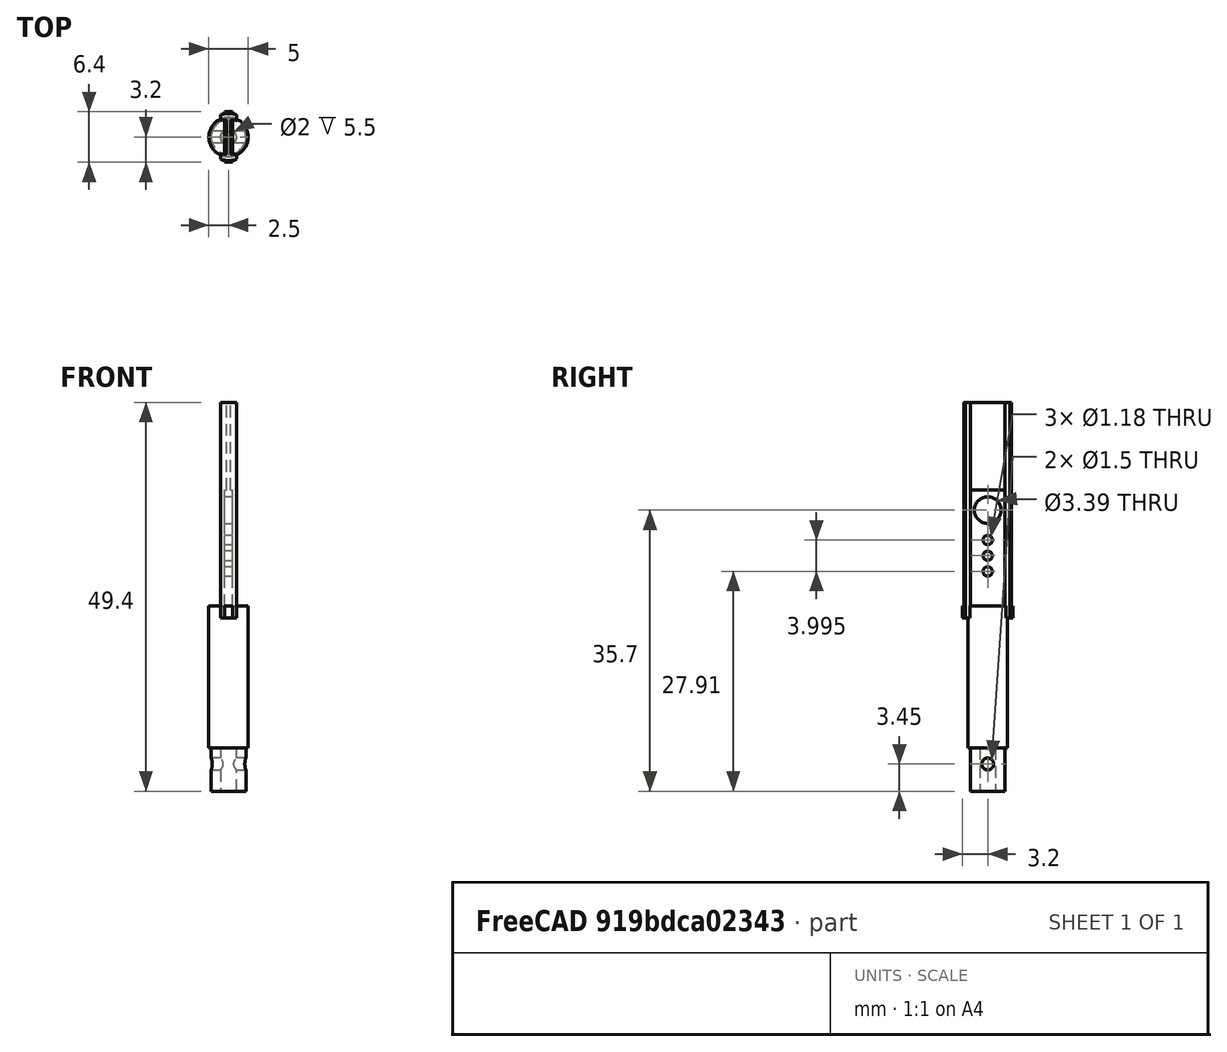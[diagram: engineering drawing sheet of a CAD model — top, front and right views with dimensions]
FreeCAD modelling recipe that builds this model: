
FCSTD DOCUMENT  (FreeCAD 0.21R33675 (Git))
Label: temholder2
License: All rights reserved
LicenseURL: http://en.wikipedia.org/wiki/All_rights_reserved
objects: TechDraw::DrawViewDimension×22, Part::Cylinder×10, TechDraw::DrawProjGroupItem×10, Part::Cut×8, Part::Box×7, Part::MultiFuse×6, TechDraw::DrawSVGTemplate×2, TechDraw::DrawProjGroup×2, TechDraw::DrawPage×2, Part::MultiCommon×1
note: 32 computed .brp shape members not serialized (recipe doc carries the construction recipe); baked Part::Feature solids carry a one-line shape summary decoded from their .brp

FEATURE [Part::Cylinder] Cylinder  label="Zylinder"
  Angle = 360
  AttacherType = Attacher::AttachEngine3D
  FirstAngle = 0
  Height = 21.5
  Placement = pos=(0,0,-0.5) rot=(0,0,1;0rad)
  Radius = 2.2
  SecondAngle = 0
FEATURE [Part::Cylinder] Cylinder001  label="Zylinder001"
  Angle = 360
  AttacherType = Attacher::AttachEngine3D
  FirstAngle = 0
  Height = 18
  Placement = pos=(0,0,5) rot=(0,0,1;0rad)
  Radius = 2.5
  SecondAngle = 0
FEATURE [Part::Cylinder] Cylinder002  label="Zylinder002"
  Angle = 360
  AttacherType = Attacher::AttachEngine3D
  FirstAngle = 0
  Height = 6.2
  Placement = pos=(-3.25,0,2.95) rot=(0,1,0;1.5708rad)
  Radius = 0.75
  SecondAngle = 0
FEATURE [Part::MultiFuse] Fusion
  Shapes = -> [Cylinder,Cylinder001]
FEATURE [Part::Cut] Cut
  Base = -> Fusion
  Tool = -> Cylinder002
FEATURE [Part::Box] Box  label="Würfel"
  AttacherType = Attacher::AttachEngine3D
  Height = 27.9
  Length = 2
  Placement = pos=(-1,-5,21) rot=(0,0,1;0rad)
  Width = 10
FEATURE [Part::Cylinder] Cylinder003  label="BeamHole"
  Angle = 360
  AttacherType = Attacher::AttachEngine3D
  FirstAngle = 0
  Height = 2
  Placement = pos=(-1,0,35.2) rot=(0,1,0;1.5708rad)
  Radius = 1.1
  SecondAngle = 0
FEATURE [Part::Cylinder] Cylinder004  label="Zylinder004"
  Angle = 360
  AttacherType = Attacher::AttachEngine3D
  FirstAngle = 0
  Height = 27.4
  Placement = pos=(0,0,21.5) rot=(0,0,1;0rad)
  Radius = 3
  SecondAngle = 0
FEATURE [Part::MultiCommon] Common
  Shapes = -> [Cylinder004,Box]
FEATURE [Part::Cut] Cut001
  Base = -> Common
  Tool = -> Cylinder003
FEATURE [Part::Cylinder] Cylinder005  label="Zylinder005"
  Angle = 360
  AttacherType = Attacher::AttachEngine3D
  FirstAngle = 0
  Height = 5.5
  Placement = pos=(0,0,-0.5) rot=(0,0,1;0rad)
  Radius = 1
  SecondAngle = 0
FEATURE [Part::Cut] Cut002
  Base = -> Cut
  Tool = -> Cylinder005
FEATURE [Part::Cylinder] Cylinder006  label="ProbeHole"
  Angle = 360
  AttacherType = Attacher::AttachEngine3D
  FirstAngle = 0
  Height = 20
  Placement = pos=(-4,0,35.2) rot=(0,1,0;1.5708rad)
  Radius = 1.695
  SecondAngle = 0
FEATURE [Part::Cut] Cut003
  Base = -> Cut001
  Tool = -> Cylinder006
FEATURE [Part::Box] Box001  label="Würfel001"
  AttacherType = Attacher::AttachEngine3D
  Height = 27
  Length = 10
  Placement = pos=(1,-2.57,21) rot=(0,0,1;0rad)
  Width = 5.5
FEATURE [Part::Cut] Cut004
  Base = -> Cut003
  Tool = -> Box001
FEATURE [Part::MultiFuse] Fusion001
  Shapes = -> [Cut002,Cut004]
FEATURE [Part::Box] Box002  label="Würfel002"
  AttacherType = Attacher::AttachEngine3D
  Height = 1.5
  Length = 1
  Placement = pos=(-0.5,-3.2,21.5) rot=(0,0,1;0rad)
  Width = 6.4
FEATURE [Part::Box] Box003  label="Würfel003"
  AttacherType = Attacher::AttachEngine3D
  Height = 26
  Length = 10
  Placement = pos=(0.5,-2.19,23) rot=(0,0,1;0rad)
  Width = 4.37
FEATURE [Part::Box] Box004  label="Würfel004"
  AttacherType = Attacher::AttachEngine3D
  Height = 26
  Length = 10
  Placement = pos=(-10.5,-2.19,23) rot=(0,0,1;0rad)
  Width = 4.37
FEATURE [Part::MultiFuse] Fusion002  label="MirrorGrooves"
  Shapes = -> [Box004,Box003]
FEATURE [Part::Cut] Cut005
  Base = -> Fusion001
  Tool = -> Fusion002
FEATURE [Part::Cylinder] Cylinder007  label="M1_6__Thread1"
  Angle = 360
  AttacherType = Attacher::AttachEngine3D
  FirstAngle = 0
  Height = 50
  Placement = pos=(-4,0,31.405) rot=(0,1,0;1.5708rad)
  Radius = 0.59
  SecondAngle = 0
FEATURE [Part::Cylinder] Cylinder008  label="M1_6__Thread2"
  Angle = 360
  AttacherType = Attacher::AttachEngine3D
  FirstAngle = 0
  Height = 50
  Placement = pos=(-4,0,29.41) rot=(0,1,0;1.5708rad)
  Radius = 0.59
  SecondAngle = 0
FEATURE [Part::Box] Box005  label="Würfel005"
  AttacherType = Attacher::AttachEngine3D
  Height = 12
  Length = 10
  Placement = pos=(0.25,-2.19,36.77) rot=(0,0,1;0rad)
  Width = 4.37
FEATURE [Part::Box] Box006  label="Würfel006"
  AttacherType = Attacher::AttachEngine3D
  Height = 12
  Length = 10
  Placement = pos=(-10.25,-2.19,36.77) rot=(0,0,1;0rad)
  Width = 4.37
FEATURE [Part::MultiFuse] Fusion004
  Placement = pos=(0,0,1) rot=(0,0,1;0rad)
  Shapes = -> [Box005,Box006]
FEATURE [TechDraw::DrawSVGTemplate] Template
  EditableTexts = Designed_by_Name=Thomas Spielauer; Drawing_number=001; FC-Date=2023-05-22; FC-SC=2:1; FC-SH=2/2; FC-Title=TEM Mirror Holder; Subtitle=Version 2023-05-22
  Height = 210
  Orientation = 1
  Width = 297
FEATURE [TechDraw::DrawSVGTemplate] Template001
  EditableTexts = Designed_by_Name=Thomas Spielauer; Drawing_number=001; FC-Date=2023-05-22; FC-SC=3:2; FC-SH=2/2; FC-Title=TEM Mirror Holder; Subtitle=Version 2023-05-22
  Height = 210
  Orientation = 1
  Width = 297
FEATURE [Part::Cylinder] Cylinder009  label="M1_6__Thread3"
  Angle = 360
  AttacherType = Attacher::AttachEngine3D
  FirstAngle = 0
  Height = 50
  Placement = pos=(-4,0,27.41) rot=(0,1,0;1.5708rad)
  Radius = 0.59
  SecondAngle = 0
FEATURE [Part::MultiFuse] Fusion003  label="MirrorMountingHoles"
  Shapes = -> [Cylinder007,Cylinder008,Cylinder009]
FEATURE [Part::Cut] Cut006
  Base = -> Cut005
  Tool = -> Fusion003
FEATURE [Part::Cut] Cut007
  Base = -> Cut006
  Tool = -> Fusion004
FEATURE [Part::MultiFuse] Fusion005
  Shapes = -> [Cut007,Box002]
FEATURE [TechDraw::DrawProjGroupItem] ProjItem  label="Front"
  CoarseView = false
  Direction = (1,0,0)
  Focus = 100
  HardHidden = false
  IsoCount = 0
  IsoHidden = false
  IsoVisible = false
  LockPosition = true
  Perspective = false
  Rotation = 0
  RotationVector = (0,1,0)
  Scale = 2
  ScaleType = 2
  ScrubCount = 0
  SeamHidden = false
  SeamVisible = true
  SmoothHidden = false
  SmoothVisible = true
  Source = -> [Fusion005]
  Type = 0
  X = 0
  XDirection = (0,-2e-16,-1)
  Y = 0
FEATURE [TechDraw::DrawProjGroupItem] ProjItem001  label="Left"
  CoarseView = false
  Direction = (1e-16,2e-16,1)
  Focus = 100
  HardHidden = false
  IsoCount = 0
  IsoHidden = false
  IsoVisible = false
  LockPosition = false
  Perspective = false
  Rotation = 0
  RotationVector = (1,0,0)
  Scale = 2
  ScaleType = 2
  ScrubCount = 0
  SeamHidden = false
  SeamVisible = true
  SmoothHidden = false
  SmoothVisible = true
  Source = -> [Fusion005]
  Type = 1
  X = 54.4
  XDirection = (1,0,-1e-16)
  Y = 0
FEATURE [TechDraw::DrawProjGroupItem] ProjItem003  label="Right"
  CoarseView = false
  Direction = (1e-16,-2e-16,-1)
  Focus = 100
  HardHidden = false
  IsoCount = 0
  IsoHidden = false
  IsoVisible = false
  LockPosition = false
  Perspective = false
  Rotation = 0
  RotationVector = (1,0,0)
  Scale = 2
  ScaleType = 2
  ScrubCount = 0
  SeamHidden = false
  SeamVisible = true
  SmoothHidden = false
  SmoothVisible = true
  Source = -> [Fusion005]
  Type = 2
  X = -54.4
  XDirection = (-1,0,-1e-16)
  Y = 0
FEATURE [TechDraw::DrawProjGroupItem] ProjItem004  label="Bottom"
  CoarseView = false
  Direction = (0,-1,2e-16)
  Focus = 100
  HardHidden = false
  IsoCount = 0
  IsoHidden = false
  IsoVisible = false
  LockPosition = false
  Perspective = false
  Rotation = 0
  RotationVector = (1,0,0)
  ScaleType = 2
  ScrubCount = 0
  SeamHidden = false
  SeamVisible = true
  SmoothHidden = false
  SmoothVisible = true
  Source = -> [Fusion005]
  Type = 5
  X = 0
  XDirection = (0,-2e-16,-1)
  Y = 41.4
FEATURE [TechDraw::DrawProjGroup] ProjGroup
  Anchor = -> ProjItem
  AutoDistribute = true
  LockPosition = false
  ProjectionType = 0
  Rotation = 0
  Scale = 2
  ScaleType = 1
  Source = -> [Fusion005]
  Views = -> [ProjItem,ProjItem001,ProjItem003,ProjItem004]
  X = 148.5
  Y = 105
  spacingX = 0
  spacingY = 30
FEATURE [TechDraw::DrawViewDimension] Dimension
  AngleOverride = false
  Arbitrary = false
  ArbitraryTolerances = false
  EqualTolerance = true
  ExtensionAngle = 0
  FormatSpec = %.2w
  FormatSpecOverTolerance = %+.2w
  FormatSpecUnderTolerance = %+.2w
  Inverted = false
  LineAngle = 0
  LockPosition = false
  MeasureType = 1
  OverTolerance = 0
  References2D = -> [ProjItem004]
  Rotation = 0
  ScaleType = 0
  TheoreticalExact = false
  Type = 0
  UnderTolerance = 0
  X = -0.570385
  Y = 36.7256
FEATURE [TechDraw::DrawViewDimension] Dimension001
  AngleOverride = false
  Arbitrary = false
  ArbitraryTolerances = false
  EqualTolerance = true
  ExtensionAngle = 0
  FormatSpec = %.2w
  FormatSpecOverTolerance = %+.2w
  FormatSpecUnderTolerance = %+.2w
  Inverted = false
  LineAngle = 0
  LockPosition = false
  MeasureType = 1
  OverTolerance = 0
  References2D = -> [ProjItem004]
  Rotation = 0
  ScaleType = 0
  TheoreticalExact = false
  Type = 0
  UnderTolerance = 0
  X = 43.2488
  Y = 27.3992
FEATURE [TechDraw::DrawViewDimension] Dimension002
  AngleOverride = false
  Arbitrary = false
  ArbitraryTolerances = false
  EqualTolerance = true
  ExtensionAngle = 0
  FormatSpec = %.2w
  FormatSpecOverTolerance = %+.2w
  FormatSpecUnderTolerance = %+.2w
  Inverted = false
  LineAngle = 0
  LockPosition = false
  MeasureType = 1
  OverTolerance = 0
  References2D = -> [ProjItem004]
  Rotation = 0
  ScaleType = 0
  TheoreticalExact = false
  Type = 0
  UnderTolerance = 0
  X = 20.4028
  Y = 27.4177
FEATURE [TechDraw::DrawViewDimension] Dimension003
  AngleOverride = false
  Arbitrary = false
  ArbitraryTolerances = false
  EqualTolerance = true
  ExtensionAngle = 0
  FormatSpec = %.2w
  FormatSpecOverTolerance = %+.2w
  FormatSpecUnderTolerance = %+.2w
  Inverted = false
  LineAngle = 0
  LockPosition = false
  MeasureType = 1
  OverTolerance = 0
  References2D = -> [ProjItem004]
  Rotation = 0
  ScaleType = 0
  TheoreticalExact = false
  Type = 0
  UnderTolerance = 0
  X = -20.5047
  Y = 16.0274
FEATURE [TechDraw::DrawViewDimension] Dimension004
  AngleOverride = false
  Arbitrary = false
  ArbitraryTolerances = false
  EqualTolerance = true
  ExtensionAngle = 0
  FormatSpec = %.2w
  FormatSpecOverTolerance = %+.2w
  FormatSpecUnderTolerance = %+.2w
  Inverted = false
  LineAngle = 0
  LockPosition = false
  MeasureType = 1
  OverTolerance = 0
  References2D = -> [ProjItem004]
  Rotation = 0
  ScaleType = 0
  TheoreticalExact = false
  Type = 0
  UnderTolerance = 0
  X = 8.18137
  Y = 19.112
FEATURE [TechDraw::DrawViewDimension] Dimension005
  AngleOverride = false
  Arbitrary = false
  ArbitraryTolerances = false
  EqualTolerance = true
  ExtensionAngle = 0
  FormatSpec = %.2w
  FormatSpecOverTolerance = %+.2w
  FormatSpecUnderTolerance = %+.2w
  Inverted = false
  LineAngle = 0
  LockPosition = false
  MeasureType = 1
  OverTolerance = 0
  References2D = -> [ProjItem004]
  Rotation = 0
  ScaleType = 0
  TheoreticalExact = false
  Type = 0
  UnderTolerance = 0
  X = 68.2961
  Y = 3.13583
FEATURE [TechDraw::DrawViewDimension] Dimension006
  AngleOverride = false
  Arbitrary = false
  ArbitraryTolerances = false
  EqualTolerance = true
  ExtensionAngle = 0
  FormatSpec = %.2w
  FormatSpecOverTolerance = %+.2w
  FormatSpecUnderTolerance = %+.2w
  Inverted = false
  LineAngle = 0
  LockPosition = false
  MeasureType = 1
  OverTolerance = 0
  References2D = -> [ProjItem004]
  Rotation = 0
  ScaleType = 0
  TheoreticalExact = false
  Type = 0
  UnderTolerance = 0
  X = 78.1774
  Y = 10.4092
FEATURE [TechDraw::DrawViewDimension] Dimension007
  AngleOverride = false
  Arbitrary = false
  ArbitraryTolerances = false
  EqualTolerance = true
  ExtensionAngle = 0
  FormatSpec = %.2w
  FormatSpecOverTolerance = %+.2w
  FormatSpecUnderTolerance = %+.2w
  Inverted = false
  LineAngle = 0
  LockPosition = false
  MeasureType = 1
  OverTolerance = 0
  References2D = -> [ProjItem004]
  Rotation = 0
  ScaleType = 0
  TheoreticalExact = false
  Type = 0
  UnderTolerance = 0
  X = -59.0159
  Y = 3.08043
FEATURE [TechDraw::DrawViewDimension] Dimension008
  AngleOverride = false
  Arbitrary = false
  ArbitraryTolerances = false
  EqualTolerance = true
  ExtensionAngle = 0
  FormatSpec = %.2w
  FormatSpecOverTolerance = %+.2w
  FormatSpecUnderTolerance = %+.2w
  Inverted = false
  LineAngle = 0
  LockPosition = false
  MeasureType = 1
  OverTolerance = 0
  References2D = -> [ProjItem004]
  Rotation = 0
  ScaleType = 0
  TheoreticalExact = false
  Type = 0
  UnderTolerance = 0
  X = 17.8117
  Y = -5.66689
FEATURE [TechDraw::DrawViewDimension] Dimension010
  AngleOverride = false
  Arbitrary = false
  ArbitraryTolerances = false
  EqualTolerance = true
  ExtensionAngle = 0
  FormatSpec = %.2w
  FormatSpecOverTolerance = %+.2w
  FormatSpecUnderTolerance = %+.2w
  Inverted = false
  LineAngle = 0
  LockPosition = false
  MeasureType = 1
  OverTolerance = 0
  References2D = -> [ProjItem]
  Rotation = 0
  ScaleType = 0
  TheoreticalExact = false
  Type = 0
  UnderTolerance = 0
  X = -80.5776
  Y = 1.58527
FEATURE [TechDraw::DrawViewDimension] Dimension011
  AngleOverride = false
  Arbitrary = false
  ArbitraryTolerances = false
  EqualTolerance = true
  ExtensionAngle = 0
  FormatSpec = %.2w
  FormatSpecOverTolerance = %+.2w
  FormatSpecUnderTolerance = %+.2w
  Inverted = false
  LineAngle = 0
  LockPosition = false
  MeasureType = 1
  OverTolerance = 0
  References2D = -> [ProjItem]
  Rotation = 0
  ScaleType = 0
  TheoreticalExact = false
  Type = 0
  UnderTolerance = 0
  X = -69.6018
  Y = 1.50597
FEATURE [TechDraw::DrawViewDimension] Dimension012
  AngleOverride = false
  Arbitrary = false
  ArbitraryTolerances = false
  EqualTolerance = true
  ExtensionAngle = 0
  FormatSpec = %.2w
  FormatSpecOverTolerance = %+.2w
  FormatSpecUnderTolerance = %+.2w
  Inverted = false
  LineAngle = 0
  LockPosition = false
  MeasureType = 1
  OverTolerance = 0
  References2D = -> [ProjItem]
  Rotation = 0
  ScaleType = 0
  TheoreticalExact = false
  Type = 0
  UnderTolerance = 0
  X = 80.5725
  Y = 4.77787
FEATURE [TechDraw::DrawViewDimension] Dimension013
  AngleOverride = false
  Arbitrary = false
  ArbitraryTolerances = false
  EqualTolerance = true
  ExtensionAngle = 0
  FormatSpec = %.2w
  FormatSpecOverTolerance = %+.2w
  FormatSpecUnderTolerance = %+.2w
  Inverted = false
  LineAngle = 0
  LockPosition = false
  MeasureType = 1
  OverTolerance = 0
  References2D = -> [ProjItem]
  Rotation = 0
  ScaleType = 0
  TheoreticalExact = false
  Type = 0
  UnderTolerance = 0
  X = 58.3431
  Y = 1.78358
FEATURE [TechDraw::DrawViewDimension] Dimension014
  AngleOverride = false
  Arbitrary = false
  ArbitraryTolerances = false
  EqualTolerance = true
  ExtensionAngle = 0
  FormatSpec = %.2w
  FormatSpecOverTolerance = %+.2w
  FormatSpecUnderTolerance = %+.2w
  Inverted = false
  LineAngle = 0
  LockPosition = false
  MeasureType = 1
  OverTolerance = 0
  References2D = -> [ProjItem]
  Rotation = 0
  ScaleType = 0
  TheoreticalExact = false
  Type = 0
  UnderTolerance = 0
  X = 69.2835
  Y = 2.85821
FEATURE [TechDraw::DrawViewDimension] Dimension015
  AngleOverride = false
  Arbitrary = false
  ArbitraryTolerances = false
  EqualTolerance = true
  ExtensionAngle = 0
  FormatSpec = ⌀%.2w
  FormatSpecOverTolerance = %+.2w
  FormatSpecUnderTolerance = %+.2w
  Inverted = false
  LineAngle = 0
  LockPosition = false
  MeasureType = 1
  OverTolerance = 0
  References2D = -> [ProjItem]
  Rotation = 0
  ScaleType = 0
  TheoreticalExact = false
  Type = 5
  UnderTolerance = 0
  X = -17.8818
  Y = -30.5126
FEATURE [TechDraw::DrawViewDimension] Dimension016
  AngleOverride = false
  Arbitrary = false
  ArbitraryTolerances = false
  EqualTolerance = true
  ExtensionAngle = 0
  FormatSpec = ⌀%.2w
  FormatSpecOverTolerance = %+.2w
  FormatSpecUnderTolerance = %+.2w
  Inverted = false
  LineAngle = 0
  LockPosition = false
  MeasureType = 1
  OverTolerance = 0
  References2D = -> [ProjItem]
  Rotation = 0
  ScaleType = 0
  TheoreticalExact = false
  Type = 5
  UnderTolerance = 0
  X = -6.5506
  Y = -20.9661
FEATURE [TechDraw::DrawViewDimension] Dimension017
  AngleOverride = false
  Arbitrary = false
  ArbitraryTolerances = false
  EqualTolerance = true
  ExtensionAngle = 0
  FormatSpec = ⌀%.2w
  FormatSpecOverTolerance = %+.2w
  FormatSpecUnderTolerance = %+.2w
  Inverted = false
  LineAngle = 0
  LockPosition = false
  MeasureType = 1
  OverTolerance = 0
  References2D = -> [ProjItem]
  Rotation = 0
  ScaleType = 0
  TheoreticalExact = false
  Type = 5
  UnderTolerance = 0
  X = 0
  Y = -20.3856
FEATURE [TechDraw::DrawViewDimension] Dimension018
  AngleOverride = false
  Arbitrary = false
  ArbitraryTolerances = false
  EqualTolerance = true
  ExtensionAngle = 0
  FormatSpec = %.2w
  FormatSpecOverTolerance = %+.2w
  FormatSpecUnderTolerance = %+.2w
  Inverted = false
  LineAngle = 0
  LockPosition = false
  MeasureType = 1
  OverTolerance = 0
  References2D = -> [ProjItem]
  Rotation = 0
  ScaleType = 0
  TheoreticalExact = false
  Type = 0
  UnderTolerance = 0
  X = 37.2627
  Y = -7.40421
FEATURE [TechDraw::DrawViewDimension] Dimension019
  AngleOverride = false
  Arbitrary = false
  ArbitraryTolerances = false
  EqualTolerance = true
  ExtensionAngle = 0
  FormatSpec = %.2w
  FormatSpecOverTolerance = %+.2w
  FormatSpecUnderTolerance = %+.2w
  Inverted = false
  LineAngle = 0
  LockPosition = false
  MeasureType = 1
  OverTolerance = 0
  References2D = -> [ProjItem001]
  Rotation = 0
  ScaleType = 0
  TheoreticalExact = false
  Type = 0
  UnderTolerance = 0
  X = 14.265
  Y = 2.24769
FEATURE [TechDraw::DrawViewDimension] Dimension020
  AngleOverride = false
  Arbitrary = false
  ArbitraryTolerances = false
  EqualTolerance = true
  ExtensionAngle = 0
  FormatSpec = ⌀%.2w
  FormatSpecOverTolerance = %+.2w
  FormatSpecUnderTolerance = %+.2w
  Inverted = false
  LineAngle = 0
  LockPosition = false
  MeasureType = 1
  OverTolerance = 0
  References2D = -> [ProjItem001]
  Rotation = 0
  ScaleType = 0
  TheoreticalExact = false
  Type = 5
  UnderTolerance = 0
  X = -8.46963
  Y = -24.8974
FEATURE [TechDraw::DrawViewDimension] Dimension021
  AngleOverride = false
  Arbitrary = false
  ArbitraryTolerances = false
  EqualTolerance = true
  ExtensionAngle = 0
  FormatSpec = %.2w
  FormatSpecOverTolerance = %+.2w
  FormatSpecUnderTolerance = %+.2w
  Inverted = false
  LineAngle = 0
  LockPosition = false
  MeasureType = 1
  OverTolerance = 0
  References2D = -> [ProjItem003]
  Rotation = 0
  ScaleType = 0
  TheoreticalExact = false
  Type = 0
  UnderTolerance = 0
  X = 0
  Y = 15.8224
FEATURE [TechDraw::DrawViewDimension] Dimension022
  AngleOverride = false
  Arbitrary = false
  ArbitraryTolerances = false
  EqualTolerance = true
  ExtensionAngle = 0
  FormatSpec = %.2w
  FormatSpecOverTolerance = %+.2w
  FormatSpecUnderTolerance = %+.2w
  Inverted = false
  LineAngle = 0
  LockPosition = false
  MeasureType = 1
  OverTolerance = 0
  References2D = -> [ProjItem003]
  Rotation = 0
  ScaleType = 0
  TheoreticalExact = false
  Type = 0
  UnderTolerance = 0
  X = -0.516427
  Y = -17.6903
FEATURE [TechDraw::DrawPage] Page
  KeepUpdated = true
  NextBalloonIndex = 1
  ProjectionType = 0
  Template = -> Template
  Views = -> [ProjGroup,Dimension,Dimension001,Dimension002,Dimension003,Dimension004,Dimension005,Dimension006,Dimension007,Dimension008,Dimension010,Dimension011,Dimension012,Dimension013,Dimension014,Dimension015,Dimension016,Dimension017,Dimension018,Dimension019,Dimension020,Dimension021,Dimension022]
FEATURE [TechDraw::DrawProjGroupItem] ProjItem005  label="Front001"
  CoarseView = false
  Direction = (0.582,-0.433,-0.688)
  Focus = 100
  HardHidden = false
  IsoCount = 0
  IsoHidden = false
  IsoVisible = false
  LockPosition = true
  Perspective = false
  Rotation = 0
  RotationVector = (-0.012,0.841,-0.54)
  Scale = 1.5
  ScaleType = 2
  ScrubCount = 0
  SeamHidden = false
  SeamVisible = true
  SmoothHidden = false
  SmoothVisible = true
  Source = -> [Fusion005]
  Type = 0
  X = 0
  XDirection = (-0.012,0.841,-0.54)
  Y = 0
FEATURE [TechDraw::DrawProjGroupItem] ProjItem006  label="FrontBottomRight"
  CoarseView = false
  Direction = (-0.140356,0.0494879,-0.988863)
  Focus = 100
  HardHidden = false
  IsoCount = 0
  IsoHidden = false
  IsoVisible = false
  LockPosition = false
  Perspective = false
  Rotation = 0
  RotationVector = (1,0,0)
  Scale = 1.5
  ScaleType = 2
  ScrubCount = 0
  SeamHidden = false
  SeamVisible = true
  SmoothHidden = false
  SmoothVisible = true
  Source = -> [Fusion005]
  Type = 9
  X = -51.338
  XDirection = (-0.420275,0.901329,0.10476)
  Y = 48.7411
FEATURE [TechDraw::DrawProjGroupItem] ProjItem007  label="FrontBottomLeft"
  CoarseView = false
  Direction = (-0.126236,-0.922281,-0.365326)
  Focus = 100
  HardHidden = false
  IsoCount = 0
  IsoHidden = false
  IsoVisible = false
  LockPosition = false
  Perspective = false
  Rotation = 0
  RotationVector = (1,0,0)
  Scale = 1.5
  ScaleType = 2
  ScrubCount = 0
  SeamHidden = false
  SeamVisible = true
  SmoothHidden = false
  SmoothVisible = true
  Source = -> [Fusion005]
  Type = 8
  X = 57.198
  XDirection = (0.40298,0.288839,-0.868435)
  Y = 48.7411
FEATURE [TechDraw::DrawProjGroupItem] ProjItem008  label="Left001"
  CoarseView = false
  Direction = (0.012229,-0.841576,0.54)
  Focus = 100
  HardHidden = false
  IsoCount = 0
  IsoHidden = false
  IsoVisible = false
  LockPosition = false
  Perspective = false
  Rotation = 0
  RotationVector = (1,0,0)
  Scale = 1.5
  ScaleType = 2
  ScrubCount = 0
  SeamHidden = false
  SeamVisible = true
  SmoothHidden = false
  SmoothVisible = true
  Source = -> [Fusion005]
  Type = 1
  X = 57.198
  XDirection = (0.582129,-0.433096,-0.688152)
  Y = 0
FEATURE [TechDraw::DrawProjGroupItem] ProjItem009  label="Right001"
  CoarseView = false
  Direction = (-0.012229,0.841576,-0.54)
  Focus = 100
  HardHidden = false
  IsoCount = 0
  IsoHidden = false
  IsoVisible = false
  LockPosition = false
  Perspective = false
  Rotation = 0
  RotationVector = (1,0,0)
  Scale = 1.5
  ScaleType = 2
  ScrubCount = 0
  SeamHidden = false
  SeamVisible = true
  SmoothHidden = false
  SmoothVisible = true
  Source = -> [Fusion005]
  Type = 2
  X = -51.338
  XDirection = (-0.582129,0.433096,0.688152)
  Y = 0
FEATURE [TechDraw::DrawProjGroupItem] ProjItem010  label="Bottom001"
  CoarseView = false
  Direction = (-0.813005,-0.322765,-0.48461)
  Focus = 100
  HardHidden = false
  IsoCount = 0
  IsoHidden = false
  IsoVisible = false
  LockPosition = false
  Perspective = false
  Rotation = 0
  RotationVector = (1,0,0)
  Scale = 1.5
  ScaleType = 2
  ScrubCount = 0
  SeamHidden = false
  SeamVisible = true
  SmoothHidden = false
  SmoothVisible = true
  Source = -> [Fusion005]
  Type = 5
  X = 0
  XDirection = (-0.012229,0.841576,-0.54)
  Y = 48.7411
FEATURE [TechDraw::DrawProjGroup] ProjGroup001
  Anchor = -> ProjItem005
  AutoDistribute = true
  LockPosition = false
  ProjectionType = 0
  Rotation = 0
  Scale = 1.5
  ScaleType = 2
  Source = -> [Fusion005]
  Views = -> [ProjItem005,ProjItem006,ProjItem007,ProjItem008,ProjItem009,ProjItem010]
  X = 148.5
  Y = 105
  spacingX = 0
  spacingY = 0
FEATURE [TechDraw::DrawPage] Page001
  KeepUpdated = true
  NextBalloonIndex = 1
  ProjectionType = 0
  Template = -> Template001
  Views = -> [ProjGroup001]
